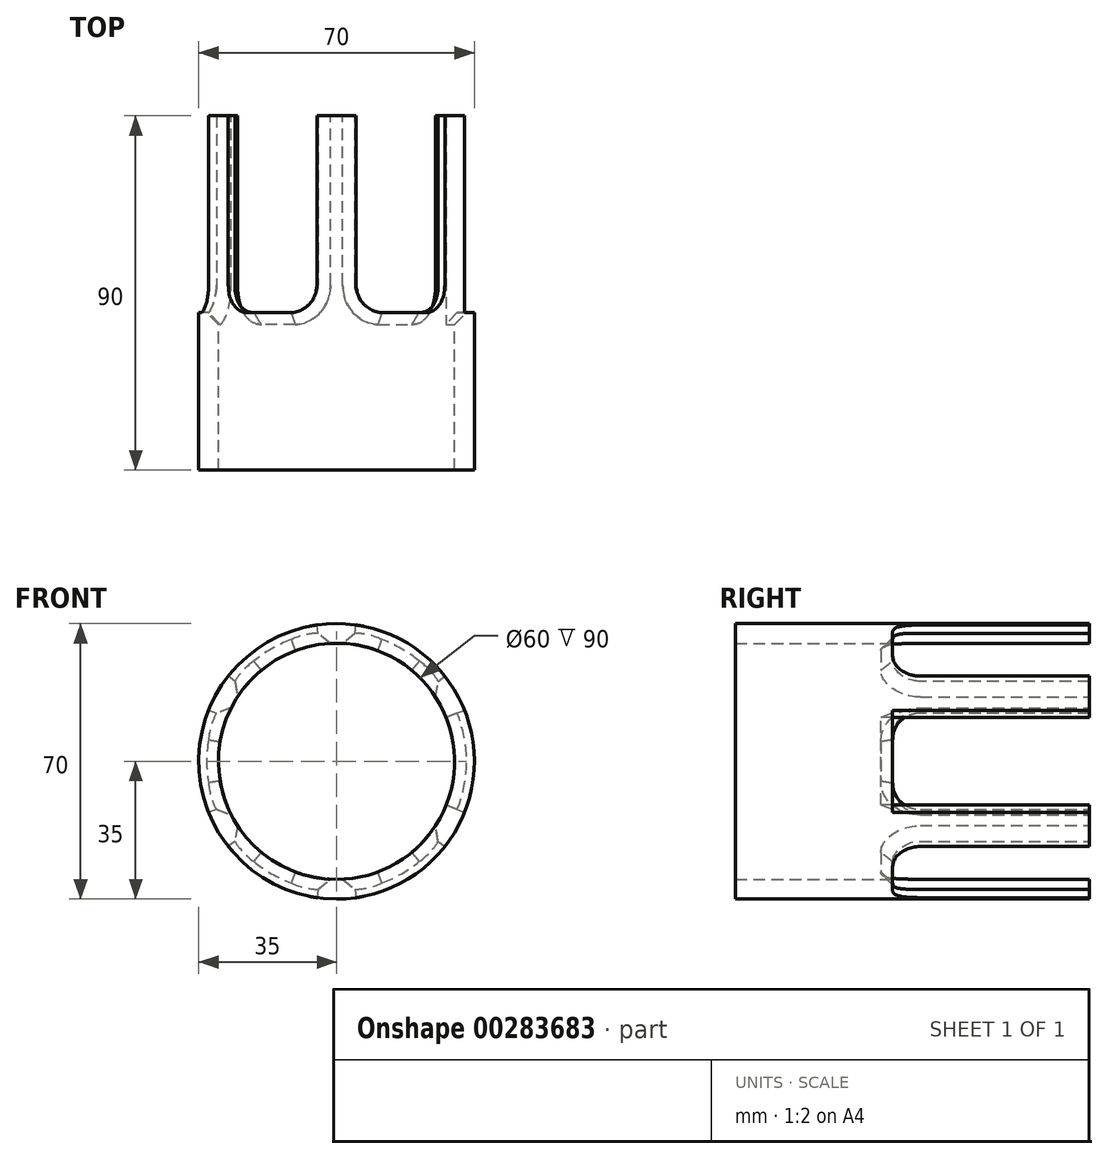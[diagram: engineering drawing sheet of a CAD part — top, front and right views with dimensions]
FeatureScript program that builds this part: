
annotation { "Feature Type Name" : "Feature", "Feature Type Description" : "" }
export const myFeature = defineFeature(function(context is Context, id is Id, definition is map)
    precondition{}
    {
        {
            var Q0;
            Q0=qCreatedBy(makeId("Front.planeOp"),FACE);
            var sketch = newSketch(context, id + "F0", { "sketchPlane" : qUnion([Q0])});
            skCircle(sketch, "E0", {"center": v(0, 0) * mm, "radius": 30 * mm});
            skCircle(sketch, "E1", {"center": v(0, 0) * mm, "radius": 35 * mm});
            skLineSegment(sketch, "E2", {"start": v(-4.29, 29.7) * mm, "end": v(-5, 34.64) * mm});
            skLineSegment(sketch, "E3", {"start": v(4.29, 29.7) * mm, "end": v(5, 34.64) * mm});
            skLineSegment(sketch, "E4.1.0", {"start": v(-27.86, 11.13) * mm, "end": v(-32.5, 13) * mm});
            skLineSegment(sketch, "E4.1.1", {"start": v(-23.57, 18.56) * mm, "end": v(-27.5, 21.65) * mm});
            skLineSegment(sketch, "E4.2.0", {"start": v(-23.57, -18.56) * mm, "end": v(-27.5, -21.65) * mm});
            skLineSegment(sketch, "E4.2.1", {"start": v(-27.86, -11.13) * mm, "end": v(-32.5, -13) * mm});
            skLineSegment(sketch, "E4.3.0", {"start": v(4.29, -29.7) * mm, "end": v(5, -34.64) * mm});
            skLineSegment(sketch, "E4.3.1", {"start": v(-4.29, -29.7) * mm, "end": v(-5, -34.64) * mm});
            skLineSegment(sketch, "E4.4.0", {"start": v(27.86, -11.13) * mm, "end": v(32.5, -13) * mm});
            skLineSegment(sketch, "E4.4.1", {"start": v(23.57, -18.56) * mm, "end": v(27.5, -21.65) * mm});
            skLineSegment(sketch, "E4.5.0", {"start": v(23.57, 18.56) * mm, "end": v(27.5, 21.65) * mm});
            skLineSegment(sketch, "E4.5.1", {"start": v(27.86, 11.13) * mm, "end": v(32.5, 13) * mm});
            skSolve(sketch);
        }
        {
            var Q0;
            {var subQ0=sQuery(id+"F0.wireOp",EDGE,"E4.1.0");Q0=makeQuery(id+"F0.imprint","IMPRINT",FACE,{"disambiguationData":[TD([[makeQuery(id+"F0.imprint","IMPRINT",EDGE,{"derivedFrom":subQ0}),-1.0]])]});}
            var Q1;
            {var subQ0=sQuery(id+"F0.wireOp",EDGE,"E2");Q1=makeQuery(id+"F0.imprint","IMPRINT",FACE,{"disambiguationData":[TD([[makeQuery(id+"F0.imprint","IMPRINT",EDGE,{"derivedFrom":subQ0}),1.0]])]});}
            var Q2;
            {var subQ0=sQuery(id+"F0.wireOp",EDGE,"E2");Q2=makeQuery(id+"F0.imprint","IMPRINT",FACE,{"disambiguationData":[TD([[makeQuery(id+"F0.imprint","IMPRINT",EDGE,{"derivedFrom":subQ0}),-1.0]])]});}
            var Q3;
            {var subQ0=sQuery(id+"F0.wireOp",EDGE,"E3");Q3=makeQuery(id+"F0.imprint","IMPRINT",FACE,{"disambiguationData":[TD([[makeQuery(id+"F0.imprint","IMPRINT",EDGE,{"derivedFrom":subQ0}),-1.0]])]});}
            var Q4;
            {var subQ0=sQuery(id+"F0.wireOp",EDGE,"E4.5.0");Q4=makeQuery(id+"F0.imprint","IMPRINT",FACE,{"disambiguationData":[TD([[makeQuery(id+"F0.imprint","IMPRINT",EDGE,{"derivedFrom":subQ0}),-1.0]])]});}
            var Q5;
            {var subQ0=sQuery(id+"F0.wireOp",EDGE,"E4.4.0");Q5=makeQuery(id+"F0.imprint","IMPRINT",FACE,{"disambiguationData":[TD([[makeQuery(id+"F0.imprint","IMPRINT",EDGE,{"derivedFrom":subQ0}),1.0]])]});}
            var Q6;
            {var subQ0=sQuery(id+"F0.wireOp",EDGE,"E4.4.0");Q6=makeQuery(id+"F0.imprint","IMPRINT",FACE,{"disambiguationData":[TD([[makeQuery(id+"F0.imprint","IMPRINT",EDGE,{"derivedFrom":subQ0}),-1.0]])]});}
            var Q7;
            {var subQ0=sQuery(id+"F0.wireOp",EDGE,"E4.3.0");Q7=makeQuery(id+"F0.imprint","IMPRINT",FACE,{"disambiguationData":[TD([[makeQuery(id+"F0.imprint","IMPRINT",EDGE,{"derivedFrom":subQ0}),1.0]])]});}
            var Q8;
            {var subQ0=sQuery(id+"F0.wireOp",EDGE,"E4.3.0");Q8=makeQuery(id+"F0.imprint","IMPRINT",FACE,{"disambiguationData":[TD([[makeQuery(id+"F0.imprint","IMPRINT",EDGE,{"derivedFrom":subQ0}),-1.0]])]});}
            var Q9;
            {var subQ0=sQuery(id+"F0.wireOp",EDGE,"E4.2.0");Q9=makeQuery(id+"F0.imprint","IMPRINT",FACE,{"disambiguationData":[TD([[makeQuery(id+"F0.imprint","IMPRINT",EDGE,{"derivedFrom":subQ0}),1.0]])]});}
            var Q10;
            {var subQ0=sQuery(id+"F0.wireOp",EDGE,"E4.2.0");Q10=makeQuery(id+"F0.imprint","IMPRINT",FACE,{"disambiguationData":[TD([[makeQuery(id+"F0.imprint","IMPRINT",EDGE,{"derivedFrom":subQ0}),-1.0]])]});}
            var Q11;
            {var subQ0=sQuery(id+"F0.wireOp",EDGE,"E4.1.0");Q11=makeQuery(id+"F0.imprint","IMPRINT",FACE,{"disambiguationData":[TD([[makeQuery(id+"F0.imprint","IMPRINT",EDGE,{"derivedFrom":subQ0}),1.0]])]});}
            extrude(context, id + "F1", {"entities" : qUnion([Q0, Q1, Q2, Q3, Q4, Q5, Q6, Q7, Q8, Q9, Q10, Q11]), "depth" : 40 * mm});
        }
        {
            var Q0;
            {var subQ0=sQuery(id+"F0.wireOp",EDGE,"E2");Q0=makeQuery(id+"F0.imprint","IMPRINT",FACE,{"disambiguationData":[TD([[makeQuery(id+"F0.imprint","IMPRINT",EDGE,{"derivedFrom":subQ0}),-1.0]])]});}
            var Q1;
            {var subQ0=sQuery(id+"F0.wireOp",EDGE,"E4.1.0");Q1=makeQuery(id+"F0.imprint","IMPRINT",FACE,{"disambiguationData":[TD([[makeQuery(id+"F0.imprint","IMPRINT",EDGE,{"derivedFrom":subQ0}),-1.0]])]});}
            var Q2;
            {var subQ0=sQuery(id+"F0.wireOp",EDGE,"E4.2.0");Q2=makeQuery(id+"F0.imprint","IMPRINT",FACE,{"disambiguationData":[TD([[makeQuery(id+"F0.imprint","IMPRINT",EDGE,{"derivedFrom":subQ0}),-1.0]])]});}
            var Q3;
            {var subQ0=sQuery(id+"F0.wireOp",EDGE,"E4.3.0");Q3=makeQuery(id+"F0.imprint","IMPRINT",FACE,{"disambiguationData":[TD([[makeQuery(id+"F0.imprint","IMPRINT",EDGE,{"derivedFrom":subQ0}),-1.0]])]});}
            var Q4;
            {var subQ0=sQuery(id+"F0.wireOp",EDGE,"E4.4.0");Q4=makeQuery(id+"F0.imprint","IMPRINT",FACE,{"disambiguationData":[TD([[makeQuery(id+"F0.imprint","IMPRINT",EDGE,{"derivedFrom":subQ0}),-1.0]])]});}
            var Q5;
            {var subQ0=sQuery(id+"F0.wireOp",EDGE,"E4.5.0");Q5=makeQuery(id+"F0.imprint","IMPRINT",FACE,{"disambiguationData":[TD([[makeQuery(id+"F0.imprint","IMPRINT",EDGE,{"derivedFrom":subQ0}),-1.0]])]});}
            extrude(context, id + "F2", {"entities" : qUnion([Q0, Q1, Q2, Q3, Q4, Q5]), "operationType" : NewBodyOperationType.ADD, "oppositeDirection" : true, "depth" : 50 * mm});
        }
        {
            var Q0;
            Q0=makeQuery(id+"F2.opExtrude","CAP_EDGE",EDGE,{"disambiguationData":[OSD([sQuery(id+"F0.wireOp",EDGE,"E4.1.1")])],"isStart":true});
            var Q1;
            Q1=makeQuery(id+"F2.opExtrude","CAP_EDGE",EDGE,{"disambiguationData":[OSD([sQuery(id+"F0.wireOp",EDGE,"E2")])],"isStart":true});
            var Q2;
            Q2=makeQuery(id+"F2.opExtrude","CAP_EDGE",EDGE,{"disambiguationData":[OSD([sQuery(id+"F0.wireOp",EDGE,"E4.1.0")])],"isStart":true});
            var Q3;
            Q3=makeQuery(id+"F2.opExtrude","CAP_EDGE",EDGE,{"disambiguationData":[OSD([sQuery(id+"F0.wireOp",EDGE,"E4.2.0")])],"isStart":true});
            var Q4;
            Q4=makeQuery(id+"F2.opExtrude","CAP_EDGE",EDGE,{"disambiguationData":[OSD([sQuery(id+"F0.wireOp",EDGE,"E4.3.1")])],"isStart":true});
            var Q5;
            Q5=makeQuery(id+"F2.opExtrude","CAP_EDGE",EDGE,{"disambiguationData":[OSD([sQuery(id+"F0.wireOp",EDGE,"E4.3.0")])],"isStart":true});
            var Q6;
            Q6=makeQuery(id+"F2.opExtrude","CAP_EDGE",EDGE,{"disambiguationData":[OSD([sQuery(id+"F0.wireOp",EDGE,"E4.4.1")])],"isStart":true});
            var Q7;
            Q7=makeQuery(id+"F2.opExtrude","CAP_EDGE",EDGE,{"disambiguationData":[OSD([sQuery(id+"F0.wireOp",EDGE,"E4.4.0")])],"isStart":true});
            var Q8;
            Q8=makeQuery(id+"F2.opExtrude","CAP_EDGE",EDGE,{"disambiguationData":[OSD([sQuery(id+"F0.wireOp",EDGE,"E4.5.1")])],"isStart":true});
            var Q9;
            Q9=makeQuery(id+"F2.opExtrude","CAP_EDGE",EDGE,{"disambiguationData":[OSD([sQuery(id+"F0.wireOp",EDGE,"E4.5.0")])],"isStart":true});
            var Q10;
            Q10=makeQuery(id+"F2.opExtrude","CAP_EDGE",EDGE,{"disambiguationData":[OSD([sQuery(id+"F0.wireOp",EDGE,"E3")])],"isStart":true});
            var Q11;
            Q11=makeQuery(id+"F2.opExtrude","CAP_EDGE",EDGE,{"disambiguationData":[OSD([sQuery(id+"F0.wireOp",EDGE,"E4.2.1")])],"isStart":true});
            fillet(context, id + "F3", {"entities" : qUnion([Q0, Q1, Q2, Q3, Q4, Q5, Q6, Q7, Q8, Q9, Q10, Q11]), "radius" : 7 * mm, "tangentPropagation" : true, "allowEdgeOverflow" : false});
        }
        {
            var Q0;
            {var subQ0=sQuery(id+"F0.wireOp",EDGE,"E0");var subQ2=sQuery(id+"F0.wireOp",EDGE,"E4.1.0");Q0=makeQuery(id+"F2.boolean.opBoolean","SPLIT",EDGE,{"disambiguationData":[TD([makeQuery(id+"F2.opExtrude","SWEPT_FACE",FACE,{"disambiguationData":[OSD([subQ2])]})])],"derivedFrom":makeQuery(id+"F1.opExtrude","CAP_EDGE",EDGE,{"disambiguationData":[OSD([subQ0])],"isStart":true})});}
            var Q1;
            {var subQ0=sQuery(id+"F0.wireOp",EDGE,"E0");var subQ1=sQuery(id+"F0.wireOp",EDGE,"E4.2.0");Q1=makeQuery(id+"F2.boolean.opBoolean","SPLIT",EDGE,{"disambiguationData":[TD([makeQuery(id+"F2.opExtrude","SWEPT_FACE",FACE,{"disambiguationData":[OSD([subQ1])]})])],"derivedFrom":makeQuery(id+"F1.opExtrude","CAP_EDGE",EDGE,{"disambiguationData":[OSD([subQ0])],"isStart":true})});}
            var Q2;
            {var subQ0=sQuery(id+"F0.wireOp",EDGE,"E2");var subQ1=sQuery(id+"F0.wireOp",EDGE,"E0");Q2=makeQuery(id+"F2.boolean.opBoolean","SPLIT",EDGE,{"disambiguationData":[TD([makeQuery(id+"F2.opExtrude","SWEPT_FACE",FACE,{"disambiguationData":[OSD([subQ0])]})])],"derivedFrom":makeQuery(id+"F1.opExtrude","CAP_EDGE",EDGE,{"disambiguationData":[OSD([subQ1])],"isStart":true})});}
            var Q3;
            {var subQ0=sQuery(id+"F0.wireOp",EDGE,"E0");var subQ1=sQuery(id+"F0.wireOp",EDGE,"E3");Q3=makeQuery(id+"F2.boolean.opBoolean","SPLIT",EDGE,{"disambiguationData":[TD([makeQuery(id+"F2.opExtrude","SWEPT_FACE",FACE,{"disambiguationData":[OSD([subQ1])]})])],"derivedFrom":makeQuery(id+"F1.opExtrude","CAP_EDGE",EDGE,{"disambiguationData":[OSD([subQ0])],"isStart":true})});}
            var Q4;
            {var subQ0=sQuery(id+"F0.wireOp",EDGE,"E0");var subQ2=sQuery(id+"F0.wireOp",EDGE,"E4.4.0");Q4=makeQuery(id+"F2.boolean.opBoolean","SPLIT",EDGE,{"disambiguationData":[TD([makeQuery(id+"F2.opExtrude","SWEPT_FACE",FACE,{"disambiguationData":[OSD([subQ2])]})])],"derivedFrom":makeQuery(id+"F1.opExtrude","CAP_EDGE",EDGE,{"disambiguationData":[OSD([subQ0])],"isStart":true})});}
            var Q5;
            {var subQ0=sQuery(id+"F0.wireOp",EDGE,"E0");var subQ2=sQuery(id+"F0.wireOp",EDGE,"E4.3.0");Q5=makeQuery(id+"F2.boolean.opBoolean","SPLIT",EDGE,{"disambiguationData":[TD([makeQuery(id+"F2.opExtrude","SWEPT_FACE",FACE,{"disambiguationData":[OSD([subQ2])]})])],"derivedFrom":makeQuery(id+"F1.opExtrude","CAP_EDGE",EDGE,{"disambiguationData":[OSD([subQ0])],"isStart":true})});}
            chamfer(context, id + "F4", {"entities" : qUnion([Q0, Q1, Q2, Q3, Q4, Q5]), "width" : 3 * mm, "tangentPropagation" : true});
        }
    });
